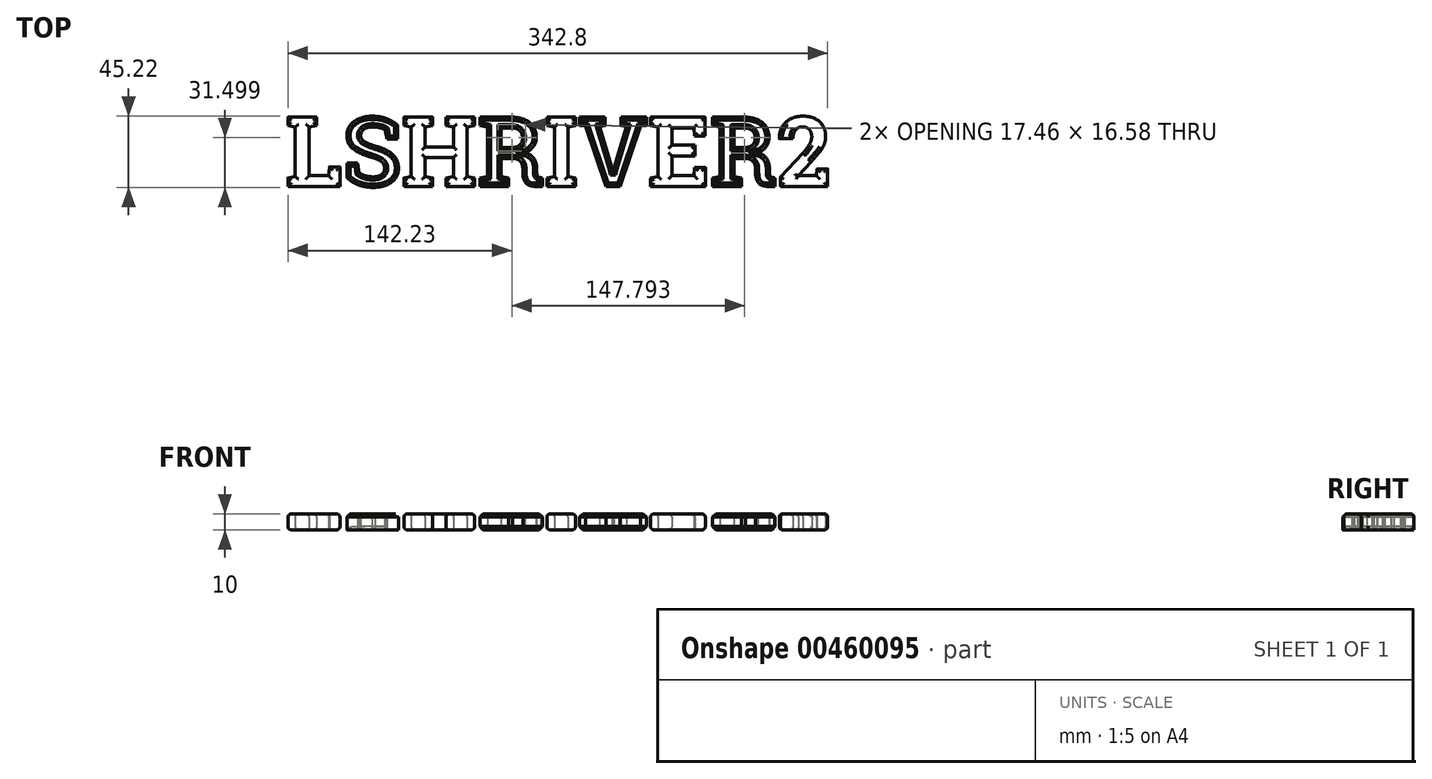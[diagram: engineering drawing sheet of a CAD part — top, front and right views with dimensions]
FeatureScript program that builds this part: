
annotation { "Feature Type Name" : "Feature", "Feature Type Description" : "" }
export const myFeature = defineFeature(function(context is Context, id is Id, definition is map)
    precondition{}
    {
        {
            var Q0;
            Q0=qCreatedBy(makeId("Top.planeOp"),FACE);
            var sketch = newSketch(context, id + "F0", { "sketchPlane" : qUnion([Q0])});
            skText(sketch, "E0", { "text": "LSHRIVER2", "fontName": "RobotoSlab-Bold.ttf"});
            const initialGuessF0  = {"E0": [-0.17416, 0, 1, 0, 0.0445]};
            skSetInitialGuess(sketch, initialGuessF0);
            skSolve(sketch);
        }
        {
            var Q0;
            Q0 = qSketchRegion(id + "F0", true);
            extrude(context, id + "F1", {"entities" : qUnion([Q0]), "depth" : 10 * mm, "offsetDistance" : 25 * mm});
        }
        {
            var Q0;
            Q0=makeQuery(id+"F1.opExtrude","CAP_FACE",FACE,{"disambiguationData":[OSD([sQuery(id+"F0.wireOp",EDGE,"E0.sketch_text.stroke-0"),sQuery(id+"F0.wireOp",EDGE,"E0.sketch_text.stroke-1"),sQuery(id+"F0.wireOp",EDGE,"E0.sketch_text.stroke-2"),sQuery(id+"F0.wireOp",EDGE,"E0.sketch_text.stroke-3"),sQuery(id+"F0.wireOp",EDGE,"E0.sketch_text.stroke-4"),sQuery(id+"F0.wireOp",EDGE,"E0.sketch_text.stroke-5"),sQuery(id+"F0.wireOp",EDGE,"E0.sketch_text.stroke-6"),sQuery(id+"F0.wireOp",EDGE,"E0.sketch_text.stroke-7"),sQuery(id+"F0.wireOp",EDGE,"E0.sketch_text.stroke-8"),sQuery(id+"F0.wireOp",EDGE,"E0.sketch_text.stroke-9"),sQuery(id+"F0.wireOp",EDGE,"E0.sketch_text.stroke-10"),sQuery(id+"F0.wireOp",EDGE,"E0.sketch_text.stroke-11"),sQuery(id+"F0.wireOp",EDGE,"E0.sketch_text.stroke-12"),sQuery(id+"F0.wireOp",EDGE,"E0.sketch_text.stroke-13"),sQuery(id+"F0.wireOp",EDGE,"E0.sketch_text.stroke-14"),sQuery(id+"F0.wireOp",EDGE,"E0.sketch_text.stroke-15")])],"isStart":false});
            var Q1;
            Q1=makeQuery(id+"F1.opExtrude","CAP_FACE",FACE,{"disambiguationData":[OSD([sQuery(id+"F0.wireOp",EDGE,"E0.sketch_text.stroke-46"),sQuery(id+"F0.wireOp",EDGE,"E0.sketch_text.stroke-47"),sQuery(id+"F0.wireOp",EDGE,"E0.sketch_text.stroke-48"),sQuery(id+"F0.wireOp",EDGE,"E0.sketch_text.stroke-49"),sQuery(id+"F0.wireOp",EDGE,"E0.sketch_text.stroke-50"),sQuery(id+"F0.wireOp",EDGE,"E0.sketch_text.stroke-51"),sQuery(id+"F0.wireOp",EDGE,"E0.sketch_text.stroke-52"),sQuery(id+"F0.wireOp",EDGE,"E0.sketch_text.stroke-53"),sQuery(id+"F0.wireOp",EDGE,"E0.sketch_text.stroke-54"),sQuery(id+"F0.wireOp",EDGE,"E0.sketch_text.stroke-55"),sQuery(id+"F0.wireOp",EDGE,"E0.sketch_text.stroke-56"),sQuery(id+"F0.wireOp",EDGE,"E0.sketch_text.stroke-57"),sQuery(id+"F0.wireOp",EDGE,"E0.sketch_text.stroke-58"),sQuery(id+"F0.wireOp",EDGE,"E0.sketch_text.stroke-59"),sQuery(id+"F0.wireOp",EDGE,"E0.sketch_text.stroke-60"),sQuery(id+"F0.wireOp",EDGE,"E0.sketch_text.stroke-61"),sQuery(id+"F0.wireOp",EDGE,"E0.sketch_text.stroke-62"),sQuery(id+"F0.wireOp",EDGE,"E0.sketch_text.stroke-63"),sQuery(id+"F0.wireOp",EDGE,"E0.sketch_text.stroke-64"),sQuery(id+"F0.wireOp",EDGE,"E0.sketch_text.stroke-65"),sQuery(id+"F0.wireOp",EDGE,"E0.sketch_text.stroke-66"),sQuery(id+"F0.wireOp",EDGE,"E0.sketch_text.stroke-67"),sQuery(id+"F0.wireOp",EDGE,"E0.sketch_text.stroke-68"),sQuery(id+"F0.wireOp",EDGE,"E0.sketch_text.stroke-69"),sQuery(id+"F0.wireOp",EDGE,"E0.sketch_text.stroke-70"),sQuery(id+"F0.wireOp",EDGE,"E0.sketch_text.stroke-71"),sQuery(id+"F0.wireOp",EDGE,"E0.sketch_text.stroke-72"),sQuery(id+"F0.wireOp",EDGE,"E0.sketch_text.stroke-73"),sQuery(id+"F0.wireOp",EDGE,"E0.sketch_text.stroke-74"),sQuery(id+"F0.wireOp",EDGE,"E0.sketch_text.stroke-75")])],"isStart":false});
            var Q2;
            Q2=makeQuery(id+"F1.opExtrude","CAP_FACE",FACE,{"disambiguationData":[OSD([sQuery(id+"F0.wireOp",EDGE,"E0.sketch_text.stroke-112"),sQuery(id+"F0.wireOp",EDGE,"E0.sketch_text.stroke-113"),sQuery(id+"F0.wireOp",EDGE,"E0.sketch_text.stroke-114"),sQuery(id+"F0.wireOp",EDGE,"E0.sketch_text.stroke-115"),sQuery(id+"F0.wireOp",EDGE,"E0.sketch_text.stroke-116"),sQuery(id+"F0.wireOp",EDGE,"E0.sketch_text.stroke-117"),sQuery(id+"F0.wireOp",EDGE,"E0.sketch_text.stroke-118"),sQuery(id+"F0.wireOp",EDGE,"E0.sketch_text.stroke-119"),sQuery(id+"F0.wireOp",EDGE,"E0.sketch_text.stroke-120"),sQuery(id+"F0.wireOp",EDGE,"E0.sketch_text.stroke-121"),sQuery(id+"F0.wireOp",EDGE,"E0.sketch_text.stroke-122"),sQuery(id+"F0.wireOp",EDGE,"E0.sketch_text.stroke-123")])],"isStart":false});
            var Q3;
            Q3=makeQuery(id+"F1.opExtrude","CAP_FACE",FACE,{"disambiguationData":[OSD([sQuery(id+"F0.wireOp",EDGE,"E0.sketch_text.stroke-142"),sQuery(id+"F0.wireOp",EDGE,"E0.sketch_text.stroke-143"),sQuery(id+"F0.wireOp",EDGE,"E0.sketch_text.stroke-144"),sQuery(id+"F0.wireOp",EDGE,"E0.sketch_text.stroke-145"),sQuery(id+"F0.wireOp",EDGE,"E0.sketch_text.stroke-146"),sQuery(id+"F0.wireOp",EDGE,"E0.sketch_text.stroke-147"),sQuery(id+"F0.wireOp",EDGE,"E0.sketch_text.stroke-148"),sQuery(id+"F0.wireOp",EDGE,"E0.sketch_text.stroke-149"),sQuery(id+"F0.wireOp",EDGE,"E0.sketch_text.stroke-150"),sQuery(id+"F0.wireOp",EDGE,"E0.sketch_text.stroke-151"),sQuery(id+"F0.wireOp",EDGE,"E0.sketch_text.stroke-152"),sQuery(id+"F0.wireOp",EDGE,"E0.sketch_text.stroke-153"),sQuery(id+"F0.wireOp",EDGE,"E0.sketch_text.stroke-154"),sQuery(id+"F0.wireOp",EDGE,"E0.sketch_text.stroke-155"),sQuery(id+"F0.wireOp",EDGE,"E0.sketch_text.stroke-156"),sQuery(id+"F0.wireOp",EDGE,"E0.sketch_text.stroke-157"),sQuery(id+"F0.wireOp",EDGE,"E0.sketch_text.stroke-158"),sQuery(id+"F0.wireOp",EDGE,"E0.sketch_text.stroke-159"),sQuery(id+"F0.wireOp",EDGE,"E0.sketch_text.stroke-160"),sQuery(id+"F0.wireOp",EDGE,"E0.sketch_text.stroke-161"),sQuery(id+"F0.wireOp",EDGE,"E0.sketch_text.stroke-162")])],"isStart":false});
            var Q4;
            Q4=makeQuery(id+"F1.opExtrude","CAP_FACE",FACE,{"disambiguationData":[OSD([sQuery(id+"F0.wireOp",EDGE,"E0.sketch_text.stroke-199"),sQuery(id+"F0.wireOp",EDGE,"E0.sketch_text.stroke-200"),sQuery(id+"F0.wireOp",EDGE,"E0.sketch_text.stroke-201"),sQuery(id+"F0.wireOp",EDGE,"E0.sketch_text.stroke-202"),sQuery(id+"F0.wireOp",EDGE,"E0.sketch_text.stroke-203"),sQuery(id+"F0.wireOp",EDGE,"E0.sketch_text.stroke-204"),sQuery(id+"F0.wireOp",EDGE,"E0.sketch_text.stroke-205"),sQuery(id+"F0.wireOp",EDGE,"E0.sketch_text.stroke-206"),sQuery(id+"F0.wireOp",EDGE,"E0.sketch_text.stroke-207"),sQuery(id+"F0.wireOp",EDGE,"E0.sketch_text.stroke-208"),sQuery(id+"F0.wireOp",EDGE,"E0.sketch_text.stroke-209"),sQuery(id+"F0.wireOp",EDGE,"E0.sketch_text.stroke-210"),sQuery(id+"F0.wireOp",EDGE,"E0.sketch_text.stroke-211"),sQuery(id+"F0.wireOp",EDGE,"E0.sketch_text.stroke-212"),sQuery(id+"F0.wireOp",EDGE,"E0.sketch_text.stroke-213"),sQuery(id+"F0.wireOp",EDGE,"E0.sketch_text.stroke-214"),sQuery(id+"F0.wireOp",EDGE,"E0.sketch_text.stroke-215"),sQuery(id+"F0.wireOp",EDGE,"E0.sketch_text.stroke-216"),sQuery(id+"F0.wireOp",EDGE,"E0.sketch_text.stroke-217"),sQuery(id+"F0.wireOp",EDGE,"E0.sketch_text.stroke-218"),sQuery(id+"F0.wireOp",EDGE,"E0.sketch_text.stroke-219"),sQuery(id+"F0.wireOp",EDGE,"E0.sketch_text.stroke-220"),sQuery(id+"F0.wireOp",EDGE,"E0.sketch_text.stroke-221")])],"isStart":false});
            var Q5;
            Q5=makeQuery(id+"F1.opExtrude","CAP_FACE",FACE,{"disambiguationData":[OSD([sQuery(id+"F0.wireOp",EDGE,"E0.sketch_text.stroke-0"),sQuery(id+"F0.wireOp",EDGE,"E0.sketch_text.stroke-1"),sQuery(id+"F0.wireOp",EDGE,"E0.sketch_text.stroke-2"),sQuery(id+"F0.wireOp",EDGE,"E0.sketch_text.stroke-3"),sQuery(id+"F0.wireOp",EDGE,"E0.sketch_text.stroke-4"),sQuery(id+"F0.wireOp",EDGE,"E0.sketch_text.stroke-5"),sQuery(id+"F0.wireOp",EDGE,"E0.sketch_text.stroke-6"),sQuery(id+"F0.wireOp",EDGE,"E0.sketch_text.stroke-7"),sQuery(id+"F0.wireOp",EDGE,"E0.sketch_text.stroke-8"),sQuery(id+"F0.wireOp",EDGE,"E0.sketch_text.stroke-9"),sQuery(id+"F0.wireOp",EDGE,"E0.sketch_text.stroke-10"),sQuery(id+"F0.wireOp",EDGE,"E0.sketch_text.stroke-11"),sQuery(id+"F0.wireOp",EDGE,"E0.sketch_text.stroke-12"),sQuery(id+"F0.wireOp",EDGE,"E0.sketch_text.stroke-13"),sQuery(id+"F0.wireOp",EDGE,"E0.sketch_text.stroke-14"),sQuery(id+"F0.wireOp",EDGE,"E0.sketch_text.stroke-15")])],"isStart":true});
            var Q6;
            Q6=makeQuery(id+"F1.opExtrude","CAP_FACE",FACE,{"disambiguationData":[OSD([sQuery(id+"F0.wireOp",EDGE,"E0.sketch_text.stroke-46"),sQuery(id+"F0.wireOp",EDGE,"E0.sketch_text.stroke-47"),sQuery(id+"F0.wireOp",EDGE,"E0.sketch_text.stroke-48"),sQuery(id+"F0.wireOp",EDGE,"E0.sketch_text.stroke-49"),sQuery(id+"F0.wireOp",EDGE,"E0.sketch_text.stroke-50"),sQuery(id+"F0.wireOp",EDGE,"E0.sketch_text.stroke-51"),sQuery(id+"F0.wireOp",EDGE,"E0.sketch_text.stroke-52"),sQuery(id+"F0.wireOp",EDGE,"E0.sketch_text.stroke-53"),sQuery(id+"F0.wireOp",EDGE,"E0.sketch_text.stroke-54"),sQuery(id+"F0.wireOp",EDGE,"E0.sketch_text.stroke-55"),sQuery(id+"F0.wireOp",EDGE,"E0.sketch_text.stroke-56"),sQuery(id+"F0.wireOp",EDGE,"E0.sketch_text.stroke-57"),sQuery(id+"F0.wireOp",EDGE,"E0.sketch_text.stroke-58"),sQuery(id+"F0.wireOp",EDGE,"E0.sketch_text.stroke-59"),sQuery(id+"F0.wireOp",EDGE,"E0.sketch_text.stroke-60"),sQuery(id+"F0.wireOp",EDGE,"E0.sketch_text.stroke-61"),sQuery(id+"F0.wireOp",EDGE,"E0.sketch_text.stroke-62"),sQuery(id+"F0.wireOp",EDGE,"E0.sketch_text.stroke-63"),sQuery(id+"F0.wireOp",EDGE,"E0.sketch_text.stroke-64"),sQuery(id+"F0.wireOp",EDGE,"E0.sketch_text.stroke-65"),sQuery(id+"F0.wireOp",EDGE,"E0.sketch_text.stroke-66"),sQuery(id+"F0.wireOp",EDGE,"E0.sketch_text.stroke-67"),sQuery(id+"F0.wireOp",EDGE,"E0.sketch_text.stroke-68"),sQuery(id+"F0.wireOp",EDGE,"E0.sketch_text.stroke-69"),sQuery(id+"F0.wireOp",EDGE,"E0.sketch_text.stroke-70"),sQuery(id+"F0.wireOp",EDGE,"E0.sketch_text.stroke-71"),sQuery(id+"F0.wireOp",EDGE,"E0.sketch_text.stroke-72"),sQuery(id+"F0.wireOp",EDGE,"E0.sketch_text.stroke-73"),sQuery(id+"F0.wireOp",EDGE,"E0.sketch_text.stroke-74"),sQuery(id+"F0.wireOp",EDGE,"E0.sketch_text.stroke-75")])],"isStart":true});
            var Q7;
            Q7=makeQuery(id+"F1.opExtrude","CAP_FACE",FACE,{"disambiguationData":[OSD([sQuery(id+"F0.wireOp",EDGE,"E0.sketch_text.stroke-112"),sQuery(id+"F0.wireOp",EDGE,"E0.sketch_text.stroke-113"),sQuery(id+"F0.wireOp",EDGE,"E0.sketch_text.stroke-114"),sQuery(id+"F0.wireOp",EDGE,"E0.sketch_text.stroke-115"),sQuery(id+"F0.wireOp",EDGE,"E0.sketch_text.stroke-116"),sQuery(id+"F0.wireOp",EDGE,"E0.sketch_text.stroke-117"),sQuery(id+"F0.wireOp",EDGE,"E0.sketch_text.stroke-118"),sQuery(id+"F0.wireOp",EDGE,"E0.sketch_text.stroke-119"),sQuery(id+"F0.wireOp",EDGE,"E0.sketch_text.stroke-120"),sQuery(id+"F0.wireOp",EDGE,"E0.sketch_text.stroke-121"),sQuery(id+"F0.wireOp",EDGE,"E0.sketch_text.stroke-122"),sQuery(id+"F0.wireOp",EDGE,"E0.sketch_text.stroke-123")])],"isStart":true});
            var Q8;
            Q8=makeQuery(id+"F1.opExtrude","CAP_FACE",FACE,{"disambiguationData":[OSD([sQuery(id+"F0.wireOp",EDGE,"E0.sketch_text.stroke-142"),sQuery(id+"F0.wireOp",EDGE,"E0.sketch_text.stroke-143"),sQuery(id+"F0.wireOp",EDGE,"E0.sketch_text.stroke-144"),sQuery(id+"F0.wireOp",EDGE,"E0.sketch_text.stroke-145"),sQuery(id+"F0.wireOp",EDGE,"E0.sketch_text.stroke-146"),sQuery(id+"F0.wireOp",EDGE,"E0.sketch_text.stroke-147"),sQuery(id+"F0.wireOp",EDGE,"E0.sketch_text.stroke-148"),sQuery(id+"F0.wireOp",EDGE,"E0.sketch_text.stroke-149"),sQuery(id+"F0.wireOp",EDGE,"E0.sketch_text.stroke-150"),sQuery(id+"F0.wireOp",EDGE,"E0.sketch_text.stroke-151"),sQuery(id+"F0.wireOp",EDGE,"E0.sketch_text.stroke-152"),sQuery(id+"F0.wireOp",EDGE,"E0.sketch_text.stroke-153"),sQuery(id+"F0.wireOp",EDGE,"E0.sketch_text.stroke-154"),sQuery(id+"F0.wireOp",EDGE,"E0.sketch_text.stroke-155"),sQuery(id+"F0.wireOp",EDGE,"E0.sketch_text.stroke-156"),sQuery(id+"F0.wireOp",EDGE,"E0.sketch_text.stroke-157"),sQuery(id+"F0.wireOp",EDGE,"E0.sketch_text.stroke-158"),sQuery(id+"F0.wireOp",EDGE,"E0.sketch_text.stroke-159"),sQuery(id+"F0.wireOp",EDGE,"E0.sketch_text.stroke-160"),sQuery(id+"F0.wireOp",EDGE,"E0.sketch_text.stroke-161"),sQuery(id+"F0.wireOp",EDGE,"E0.sketch_text.stroke-162")])],"isStart":true});
            var Q9;
            Q9=makeQuery(id+"F1.opExtrude","CAP_FACE",FACE,{"disambiguationData":[OSD([sQuery(id+"F0.wireOp",EDGE,"E0.sketch_text.stroke-199"),sQuery(id+"F0.wireOp",EDGE,"E0.sketch_text.stroke-200"),sQuery(id+"F0.wireOp",EDGE,"E0.sketch_text.stroke-201"),sQuery(id+"F0.wireOp",EDGE,"E0.sketch_text.stroke-202"),sQuery(id+"F0.wireOp",EDGE,"E0.sketch_text.stroke-203"),sQuery(id+"F0.wireOp",EDGE,"E0.sketch_text.stroke-204"),sQuery(id+"F0.wireOp",EDGE,"E0.sketch_text.stroke-205"),sQuery(id+"F0.wireOp",EDGE,"E0.sketch_text.stroke-206"),sQuery(id+"F0.wireOp",EDGE,"E0.sketch_text.stroke-207"),sQuery(id+"F0.wireOp",EDGE,"E0.sketch_text.stroke-208"),sQuery(id+"F0.wireOp",EDGE,"E0.sketch_text.stroke-209"),sQuery(id+"F0.wireOp",EDGE,"E0.sketch_text.stroke-210"),sQuery(id+"F0.wireOp",EDGE,"E0.sketch_text.stroke-211"),sQuery(id+"F0.wireOp",EDGE,"E0.sketch_text.stroke-212"),sQuery(id+"F0.wireOp",EDGE,"E0.sketch_text.stroke-213"),sQuery(id+"F0.wireOp",EDGE,"E0.sketch_text.stroke-214"),sQuery(id+"F0.wireOp",EDGE,"E0.sketch_text.stroke-215"),sQuery(id+"F0.wireOp",EDGE,"E0.sketch_text.stroke-216"),sQuery(id+"F0.wireOp",EDGE,"E0.sketch_text.stroke-217"),sQuery(id+"F0.wireOp",EDGE,"E0.sketch_text.stroke-218"),sQuery(id+"F0.wireOp",EDGE,"E0.sketch_text.stroke-219"),sQuery(id+"F0.wireOp",EDGE,"E0.sketch_text.stroke-220"),sQuery(id+"F0.wireOp",EDGE,"E0.sketch_text.stroke-221")])],"isStart":true});
            fillet(context, id + "F2", {"entities" : qUnion([Q0, Q1, Q2, Q3, Q4, Q5, Q6, Q7, Q8, Q9]), "tangentPropagation" : true, "radius" : 2 * mm, "defaultsChanged" : false, "vertexSettings" : [], "allowEdgeOverflow" : false});
        }
        {
            var Q0;
            Q0=makeQuery(id+"F1.opExtrude","CAP_FACE",FACE,{"disambiguationData":[OSD([sQuery(id+"F0.wireOp",EDGE,"E0.sketch_text.stroke-16"),sQuery(id+"F0.wireOp",EDGE,"E0.sketch_text.stroke-17"),sQuery(id+"F0.wireOp",EDGE,"E0.sketch_text.stroke-18"),sQuery(id+"F0.wireOp",EDGE,"E0.sketch_text.stroke-19"),sQuery(id+"F0.wireOp",EDGE,"E0.sketch_text.stroke-20"),sQuery(id+"F0.wireOp",EDGE,"E0.sketch_text.stroke-21"),sQuery(id+"F0.wireOp",EDGE,"E0.sketch_text.stroke-22"),sQuery(id+"F0.wireOp",EDGE,"E0.sketch_text.stroke-23"),sQuery(id+"F0.wireOp",EDGE,"E0.sketch_text.stroke-24"),sQuery(id+"F0.wireOp",EDGE,"E0.sketch_text.stroke-25"),sQuery(id+"F0.wireOp",EDGE,"E0.sketch_text.stroke-26"),sQuery(id+"F0.wireOp",EDGE,"E0.sketch_text.stroke-27"),sQuery(id+"F0.wireOp",EDGE,"E0.sketch_text.stroke-28"),sQuery(id+"F0.wireOp",EDGE,"E0.sketch_text.stroke-29"),sQuery(id+"F0.wireOp",EDGE,"E0.sketch_text.stroke-30"),sQuery(id+"F0.wireOp",EDGE,"E0.sketch_text.stroke-31"),sQuery(id+"F0.wireOp",EDGE,"E0.sketch_text.stroke-32"),sQuery(id+"F0.wireOp",EDGE,"E0.sketch_text.stroke-33"),sQuery(id+"F0.wireOp",EDGE,"E0.sketch_text.stroke-34"),sQuery(id+"F0.wireOp",EDGE,"E0.sketch_text.stroke-35"),sQuery(id+"F0.wireOp",EDGE,"E0.sketch_text.stroke-36"),sQuery(id+"F0.wireOp",EDGE,"E0.sketch_text.stroke-37"),sQuery(id+"F0.wireOp",EDGE,"E0.sketch_text.stroke-38"),sQuery(id+"F0.wireOp",EDGE,"E0.sketch_text.stroke-39"),sQuery(id+"F0.wireOp",EDGE,"E0.sketch_text.stroke-40"),sQuery(id+"F0.wireOp",EDGE,"E0.sketch_text.stroke-41"),sQuery(id+"F0.wireOp",EDGE,"E0.sketch_text.stroke-42"),sQuery(id+"F0.wireOp",EDGE,"E0.sketch_text.stroke-43"),sQuery(id+"F0.wireOp",EDGE,"E0.sketch_text.stroke-44"),sQuery(id+"F0.wireOp",EDGE,"E0.sketch_text.stroke-45")])],"isStart":false});
            var Q1;
            Q1=makeQuery(id+"F1.opExtrude","CAP_FACE",FACE,{"disambiguationData":[OSD([sQuery(id+"F0.wireOp",EDGE,"E0.sketch_text.stroke-76"),sQuery(id+"F0.wireOp",EDGE,"E0.sketch_text.stroke-77"),sQuery(id+"F0.wireOp",EDGE,"E0.sketch_text.stroke-78"),sQuery(id+"F0.wireOp",EDGE,"E0.sketch_text.stroke-79"),sQuery(id+"F0.wireOp",EDGE,"E0.sketch_text.stroke-80"),sQuery(id+"F0.wireOp",EDGE,"E0.sketch_text.stroke-81"),sQuery(id+"F0.wireOp",EDGE,"E0.sketch_text.stroke-82"),sQuery(id+"F0.wireOp",EDGE,"E0.sketch_text.stroke-83"),sQuery(id+"F0.wireOp",EDGE,"E0.sketch_text.stroke-84"),sQuery(id+"F0.wireOp",EDGE,"E0.sketch_text.stroke-85"),sQuery(id+"F0.wireOp",EDGE,"E0.sketch_text.stroke-86"),sQuery(id+"F0.wireOp",EDGE,"E0.sketch_text.stroke-87"),sQuery(id+"F0.wireOp",EDGE,"E0.sketch_text.stroke-88"),sQuery(id+"F0.wireOp",EDGE,"E0.sketch_text.stroke-89"),sQuery(id+"F0.wireOp",EDGE,"E0.sketch_text.stroke-90"),sQuery(id+"F0.wireOp",EDGE,"E0.sketch_text.stroke-91"),sQuery(id+"F0.wireOp",EDGE,"E0.sketch_text.stroke-92"),sQuery(id+"F0.wireOp",EDGE,"E0.sketch_text.stroke-93"),sQuery(id+"F0.wireOp",EDGE,"E0.sketch_text.stroke-94"),sQuery(id+"F0.wireOp",EDGE,"E0.sketch_text.stroke-95"),sQuery(id+"F0.wireOp",EDGE,"E0.sketch_text.stroke-96"),sQuery(id+"F0.wireOp",EDGE,"E0.sketch_text.stroke-97"),sQuery(id+"F0.wireOp",EDGE,"E0.sketch_text.stroke-98"),sQuery(id+"F0.wireOp",EDGE,"E0.sketch_text.stroke-99"),sQuery(id+"F0.wireOp",EDGE,"E0.sketch_text.stroke-100"),sQuery(id+"F0.wireOp",EDGE,"E0.sketch_text.stroke-101"),sQuery(id+"F0.wireOp",EDGE,"E0.sketch_text.stroke-102"),sQuery(id+"F0.wireOp",EDGE,"E0.sketch_text.stroke-103"),sQuery(id+"F0.wireOp",EDGE,"E0.sketch_text.stroke-104"),sQuery(id+"F0.wireOp",EDGE,"E0.sketch_text.stroke-105"),sQuery(id+"F0.wireOp",EDGE,"E0.sketch_text.stroke-106"),sQuery(id+"F0.wireOp",EDGE,"E0.sketch_text.stroke-107"),sQuery(id+"F0.wireOp",EDGE,"E0.sketch_text.stroke-108"),sQuery(id+"F0.wireOp",EDGE,"E0.sketch_text.stroke-109"),sQuery(id+"F0.wireOp",EDGE,"E0.sketch_text.stroke-110"),sQuery(id+"F0.wireOp",EDGE,"E0.sketch_text.stroke-111")])],"isStart":false});
            var Q2;
            Q2=makeQuery(id+"F1.opExtrude","CAP_FACE",FACE,{"disambiguationData":[OSD([sQuery(id+"F0.wireOp",EDGE,"E0.sketch_text.stroke-124"),sQuery(id+"F0.wireOp",EDGE,"E0.sketch_text.stroke-125"),sQuery(id+"F0.wireOp",EDGE,"E0.sketch_text.stroke-126"),sQuery(id+"F0.wireOp",EDGE,"E0.sketch_text.stroke-127"),sQuery(id+"F0.wireOp",EDGE,"E0.sketch_text.stroke-128"),sQuery(id+"F0.wireOp",EDGE,"E0.sketch_text.stroke-129"),sQuery(id+"F0.wireOp",EDGE,"E0.sketch_text.stroke-130"),sQuery(id+"F0.wireOp",EDGE,"E0.sketch_text.stroke-131"),sQuery(id+"F0.wireOp",EDGE,"E0.sketch_text.stroke-132"),sQuery(id+"F0.wireOp",EDGE,"E0.sketch_text.stroke-133"),sQuery(id+"F0.wireOp",EDGE,"E0.sketch_text.stroke-134"),sQuery(id+"F0.wireOp",EDGE,"E0.sketch_text.stroke-135"),sQuery(id+"F0.wireOp",EDGE,"E0.sketch_text.stroke-136"),sQuery(id+"F0.wireOp",EDGE,"E0.sketch_text.stroke-137"),sQuery(id+"F0.wireOp",EDGE,"E0.sketch_text.stroke-138"),sQuery(id+"F0.wireOp",EDGE,"E0.sketch_text.stroke-139"),sQuery(id+"F0.wireOp",EDGE,"E0.sketch_text.stroke-140"),sQuery(id+"F0.wireOp",EDGE,"E0.sketch_text.stroke-141")])],"isStart":false});
            var Q3;
            Q3=makeQuery(id+"F1.opExtrude","CAP_FACE",FACE,{"disambiguationData":[OSD([sQuery(id+"F0.wireOp",EDGE,"E0.sketch_text.stroke-163"),sQuery(id+"F0.wireOp",EDGE,"E0.sketch_text.stroke-164"),sQuery(id+"F0.wireOp",EDGE,"E0.sketch_text.stroke-165"),sQuery(id+"F0.wireOp",EDGE,"E0.sketch_text.stroke-166"),sQuery(id+"F0.wireOp",EDGE,"E0.sketch_text.stroke-167"),sQuery(id+"F0.wireOp",EDGE,"E0.sketch_text.stroke-168"),sQuery(id+"F0.wireOp",EDGE,"E0.sketch_text.stroke-169"),sQuery(id+"F0.wireOp",EDGE,"E0.sketch_text.stroke-170"),sQuery(id+"F0.wireOp",EDGE,"E0.sketch_text.stroke-171"),sQuery(id+"F0.wireOp",EDGE,"E0.sketch_text.stroke-172"),sQuery(id+"F0.wireOp",EDGE,"E0.sketch_text.stroke-173"),sQuery(id+"F0.wireOp",EDGE,"E0.sketch_text.stroke-174"),sQuery(id+"F0.wireOp",EDGE,"E0.sketch_text.stroke-175"),sQuery(id+"F0.wireOp",EDGE,"E0.sketch_text.stroke-176"),sQuery(id+"F0.wireOp",EDGE,"E0.sketch_text.stroke-177"),sQuery(id+"F0.wireOp",EDGE,"E0.sketch_text.stroke-178"),sQuery(id+"F0.wireOp",EDGE,"E0.sketch_text.stroke-179"),sQuery(id+"F0.wireOp",EDGE,"E0.sketch_text.stroke-180"),sQuery(id+"F0.wireOp",EDGE,"E0.sketch_text.stroke-181"),sQuery(id+"F0.wireOp",EDGE,"E0.sketch_text.stroke-182"),sQuery(id+"F0.wireOp",EDGE,"E0.sketch_text.stroke-183"),sQuery(id+"F0.wireOp",EDGE,"E0.sketch_text.stroke-184"),sQuery(id+"F0.wireOp",EDGE,"E0.sketch_text.stroke-185"),sQuery(id+"F0.wireOp",EDGE,"E0.sketch_text.stroke-186"),sQuery(id+"F0.wireOp",EDGE,"E0.sketch_text.stroke-187"),sQuery(id+"F0.wireOp",EDGE,"E0.sketch_text.stroke-188"),sQuery(id+"F0.wireOp",EDGE,"E0.sketch_text.stroke-189"),sQuery(id+"F0.wireOp",EDGE,"E0.sketch_text.stroke-190"),sQuery(id+"F0.wireOp",EDGE,"E0.sketch_text.stroke-191"),sQuery(id+"F0.wireOp",EDGE,"E0.sketch_text.stroke-192"),sQuery(id+"F0.wireOp",EDGE,"E0.sketch_text.stroke-193"),sQuery(id+"F0.wireOp",EDGE,"E0.sketch_text.stroke-194"),sQuery(id+"F0.wireOp",EDGE,"E0.sketch_text.stroke-195"),sQuery(id+"F0.wireOp",EDGE,"E0.sketch_text.stroke-196"),sQuery(id+"F0.wireOp",EDGE,"E0.sketch_text.stroke-197"),sQuery(id+"F0.wireOp",EDGE,"E0.sketch_text.stroke-198")])],"isStart":false});
            var Q4;
            Q4=makeQuery(id+"F1.opExtrude","CAP_FACE",FACE,{"disambiguationData":[OSD([sQuery(id+"F0.wireOp",EDGE,"E0.sketch_text.stroke-163"),sQuery(id+"F0.wireOp",EDGE,"E0.sketch_text.stroke-164"),sQuery(id+"F0.wireOp",EDGE,"E0.sketch_text.stroke-165"),sQuery(id+"F0.wireOp",EDGE,"E0.sketch_text.stroke-166"),sQuery(id+"F0.wireOp",EDGE,"E0.sketch_text.stroke-167"),sQuery(id+"F0.wireOp",EDGE,"E0.sketch_text.stroke-168"),sQuery(id+"F0.wireOp",EDGE,"E0.sketch_text.stroke-169"),sQuery(id+"F0.wireOp",EDGE,"E0.sketch_text.stroke-170"),sQuery(id+"F0.wireOp",EDGE,"E0.sketch_text.stroke-171"),sQuery(id+"F0.wireOp",EDGE,"E0.sketch_text.stroke-172"),sQuery(id+"F0.wireOp",EDGE,"E0.sketch_text.stroke-173"),sQuery(id+"F0.wireOp",EDGE,"E0.sketch_text.stroke-174"),sQuery(id+"F0.wireOp",EDGE,"E0.sketch_text.stroke-175"),sQuery(id+"F0.wireOp",EDGE,"E0.sketch_text.stroke-176"),sQuery(id+"F0.wireOp",EDGE,"E0.sketch_text.stroke-177"),sQuery(id+"F0.wireOp",EDGE,"E0.sketch_text.stroke-178"),sQuery(id+"F0.wireOp",EDGE,"E0.sketch_text.stroke-179"),sQuery(id+"F0.wireOp",EDGE,"E0.sketch_text.stroke-180"),sQuery(id+"F0.wireOp",EDGE,"E0.sketch_text.stroke-181"),sQuery(id+"F0.wireOp",EDGE,"E0.sketch_text.stroke-182"),sQuery(id+"F0.wireOp",EDGE,"E0.sketch_text.stroke-183"),sQuery(id+"F0.wireOp",EDGE,"E0.sketch_text.stroke-184"),sQuery(id+"F0.wireOp",EDGE,"E0.sketch_text.stroke-185"),sQuery(id+"F0.wireOp",EDGE,"E0.sketch_text.stroke-186"),sQuery(id+"F0.wireOp",EDGE,"E0.sketch_text.stroke-187"),sQuery(id+"F0.wireOp",EDGE,"E0.sketch_text.stroke-188"),sQuery(id+"F0.wireOp",EDGE,"E0.sketch_text.stroke-189"),sQuery(id+"F0.wireOp",EDGE,"E0.sketch_text.stroke-190"),sQuery(id+"F0.wireOp",EDGE,"E0.sketch_text.stroke-191"),sQuery(id+"F0.wireOp",EDGE,"E0.sketch_text.stroke-192"),sQuery(id+"F0.wireOp",EDGE,"E0.sketch_text.stroke-193"),sQuery(id+"F0.wireOp",EDGE,"E0.sketch_text.stroke-194"),sQuery(id+"F0.wireOp",EDGE,"E0.sketch_text.stroke-195"),sQuery(id+"F0.wireOp",EDGE,"E0.sketch_text.stroke-196"),sQuery(id+"F0.wireOp",EDGE,"E0.sketch_text.stroke-197"),sQuery(id+"F0.wireOp",EDGE,"E0.sketch_text.stroke-198")])],"isStart":true});
            var Q5;
            Q5=makeQuery(id+"F1.opExtrude","CAP_FACE",FACE,{"disambiguationData":[OSD([sQuery(id+"F0.wireOp",EDGE,"E0.sketch_text.stroke-124"),sQuery(id+"F0.wireOp",EDGE,"E0.sketch_text.stroke-125"),sQuery(id+"F0.wireOp",EDGE,"E0.sketch_text.stroke-126"),sQuery(id+"F0.wireOp",EDGE,"E0.sketch_text.stroke-127"),sQuery(id+"F0.wireOp",EDGE,"E0.sketch_text.stroke-128"),sQuery(id+"F0.wireOp",EDGE,"E0.sketch_text.stroke-129"),sQuery(id+"F0.wireOp",EDGE,"E0.sketch_text.stroke-130"),sQuery(id+"F0.wireOp",EDGE,"E0.sketch_text.stroke-131"),sQuery(id+"F0.wireOp",EDGE,"E0.sketch_text.stroke-132"),sQuery(id+"F0.wireOp",EDGE,"E0.sketch_text.stroke-133"),sQuery(id+"F0.wireOp",EDGE,"E0.sketch_text.stroke-134"),sQuery(id+"F0.wireOp",EDGE,"E0.sketch_text.stroke-135"),sQuery(id+"F0.wireOp",EDGE,"E0.sketch_text.stroke-136"),sQuery(id+"F0.wireOp",EDGE,"E0.sketch_text.stroke-137"),sQuery(id+"F0.wireOp",EDGE,"E0.sketch_text.stroke-138"),sQuery(id+"F0.wireOp",EDGE,"E0.sketch_text.stroke-139"),sQuery(id+"F0.wireOp",EDGE,"E0.sketch_text.stroke-140"),sQuery(id+"F0.wireOp",EDGE,"E0.sketch_text.stroke-141")])],"isStart":true});
            var Q6;
            Q6=makeQuery(id+"F1.opExtrude","CAP_FACE",FACE,{"disambiguationData":[OSD([sQuery(id+"F0.wireOp",EDGE,"E0.sketch_text.stroke-76"),sQuery(id+"F0.wireOp",EDGE,"E0.sketch_text.stroke-77"),sQuery(id+"F0.wireOp",EDGE,"E0.sketch_text.stroke-78"),sQuery(id+"F0.wireOp",EDGE,"E0.sketch_text.stroke-79"),sQuery(id+"F0.wireOp",EDGE,"E0.sketch_text.stroke-80"),sQuery(id+"F0.wireOp",EDGE,"E0.sketch_text.stroke-81"),sQuery(id+"F0.wireOp",EDGE,"E0.sketch_text.stroke-82"),sQuery(id+"F0.wireOp",EDGE,"E0.sketch_text.stroke-83"),sQuery(id+"F0.wireOp",EDGE,"E0.sketch_text.stroke-84"),sQuery(id+"F0.wireOp",EDGE,"E0.sketch_text.stroke-85"),sQuery(id+"F0.wireOp",EDGE,"E0.sketch_text.stroke-86"),sQuery(id+"F0.wireOp",EDGE,"E0.sketch_text.stroke-87"),sQuery(id+"F0.wireOp",EDGE,"E0.sketch_text.stroke-88"),sQuery(id+"F0.wireOp",EDGE,"E0.sketch_text.stroke-89"),sQuery(id+"F0.wireOp",EDGE,"E0.sketch_text.stroke-90"),sQuery(id+"F0.wireOp",EDGE,"E0.sketch_text.stroke-91"),sQuery(id+"F0.wireOp",EDGE,"E0.sketch_text.stroke-92"),sQuery(id+"F0.wireOp",EDGE,"E0.sketch_text.stroke-93"),sQuery(id+"F0.wireOp",EDGE,"E0.sketch_text.stroke-94"),sQuery(id+"F0.wireOp",EDGE,"E0.sketch_text.stroke-95"),sQuery(id+"F0.wireOp",EDGE,"E0.sketch_text.stroke-96"),sQuery(id+"F0.wireOp",EDGE,"E0.sketch_text.stroke-97"),sQuery(id+"F0.wireOp",EDGE,"E0.sketch_text.stroke-98"),sQuery(id+"F0.wireOp",EDGE,"E0.sketch_text.stroke-99"),sQuery(id+"F0.wireOp",EDGE,"E0.sketch_text.stroke-100"),sQuery(id+"F0.wireOp",EDGE,"E0.sketch_text.stroke-101"),sQuery(id+"F0.wireOp",EDGE,"E0.sketch_text.stroke-102"),sQuery(id+"F0.wireOp",EDGE,"E0.sketch_text.stroke-103"),sQuery(id+"F0.wireOp",EDGE,"E0.sketch_text.stroke-104"),sQuery(id+"F0.wireOp",EDGE,"E0.sketch_text.stroke-105"),sQuery(id+"F0.wireOp",EDGE,"E0.sketch_text.stroke-106"),sQuery(id+"F0.wireOp",EDGE,"E0.sketch_text.stroke-107"),sQuery(id+"F0.wireOp",EDGE,"E0.sketch_text.stroke-108"),sQuery(id+"F0.wireOp",EDGE,"E0.sketch_text.stroke-109"),sQuery(id+"F0.wireOp",EDGE,"E0.sketch_text.stroke-110"),sQuery(id+"F0.wireOp",EDGE,"E0.sketch_text.stroke-111")])],"isStart":true});
            var Q7;
            Q7=makeQuery(id+"F1.opExtrude","CAP_EDGE",EDGE,{"disambiguationData":[OSD([sQuery(id+"F0.wireOp",EDGE,"E0.sketch_text.stroke-38")])],"isStart":true});
            chamfer(context, id + "F3", {"entities" : qUnion([Q0, Q1, Q2, Q3, Q4, Q5, Q6, Q7]), "width" : 2 * mm, "tangentPropagation" : true});
        }
    });
